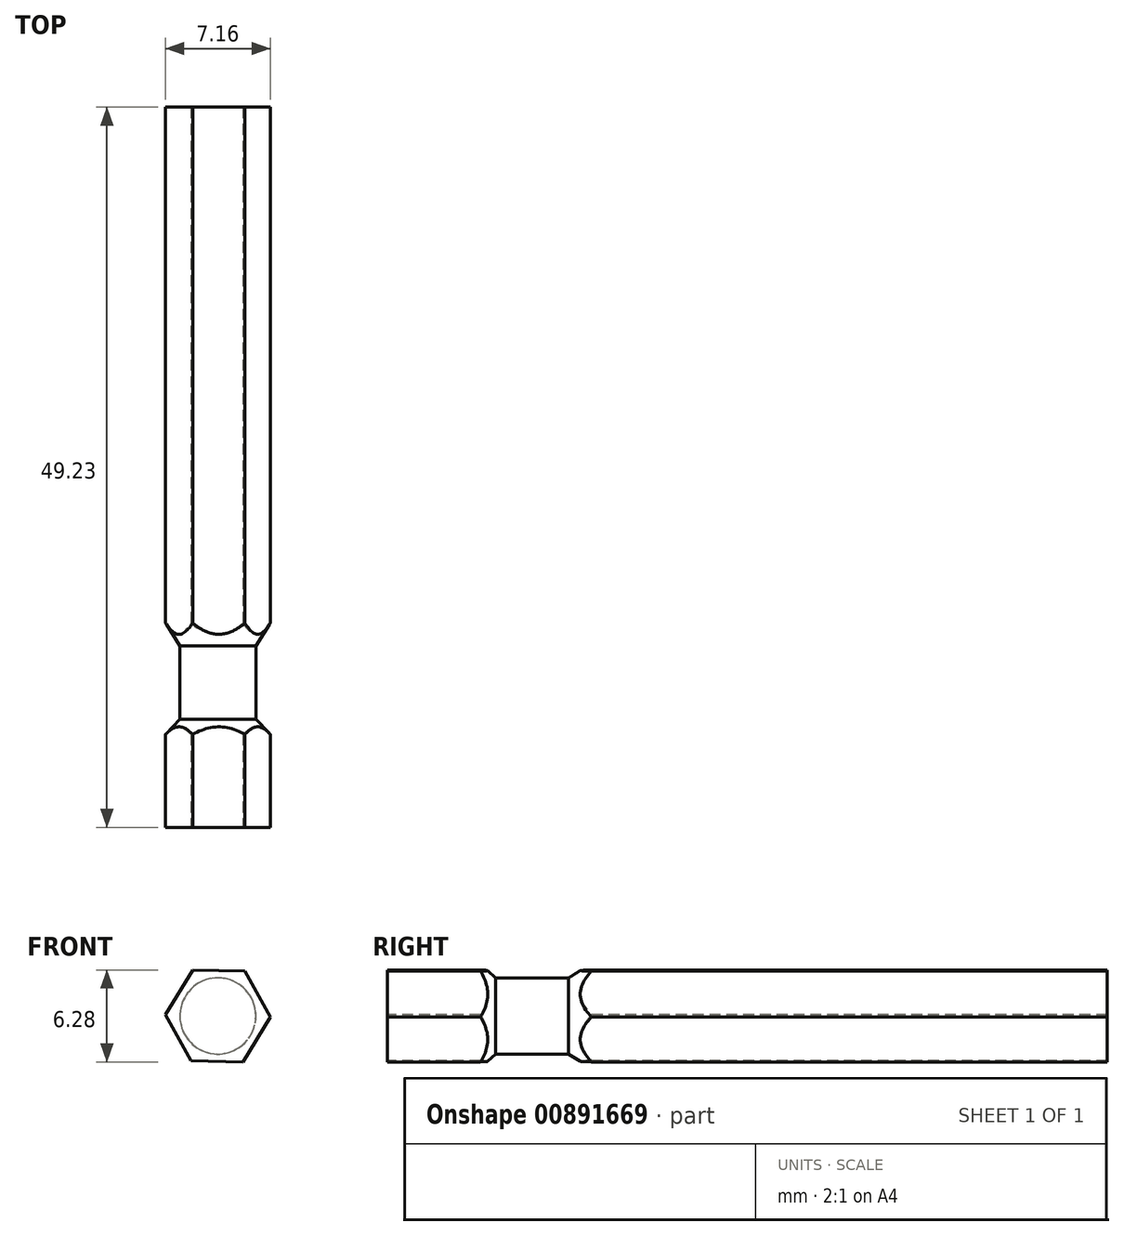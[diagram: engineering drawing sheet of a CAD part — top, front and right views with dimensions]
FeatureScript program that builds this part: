
annotation { "Feature Type Name" : "Feature", "Feature Type Description" : "" }
export const myFeature = defineFeature(function(context is Context, id is Id, definition is map)
    precondition{}
    {
        {
            var Q0;
            Q0=qCreatedBy(makeId("Top.planeOp"),FACE);
            var sketch = newSketch(context, id + "F0", { "sketchPlane" : qUnion([Q0])});
            skLineSegment(sketch, "E0.top", {"start": v(-3.75, -17.5) * mm, "end": v(3.75, -17.5) * mm});
            skLineSegment(sketch, "E0.left", {"start": v(-3.75, 17.5) * mm, "end": v(-3.75, -3.27) * mm});
            skLineSegment(sketch, "E0.right", {"start": v(3.75, 17.5) * mm, "end": v(3.75, -3.27) * mm});
            skPoint(sketch, "E0.middle", {"position": v(0, 0) * mm});
            skLineSegment(sketch, "E1", {"start": v(-2.6, -10.1) * mm, "end": v(2.6, -10.1) * mm});
            skLineSegment(sketch, "E2.bottom", {"start": v(2.6, -10.1) * mm, "end": v(-2.6, -10.1) * mm});
            skLineSegment(sketch, "E2.top", {"start": v(2.6, -5.1) * mm, "end": v(-2.6, -5.1) * mm});
            skLineSegment(sketch, "E2.left", {"start": v(2.6, -10.1) * mm, "end": v(2.6, -5.1) * mm});
            skLineSegment(sketch, "E2.right", {"start": v(-2.6, -10.1) * mm, "end": v(-2.6, -5.1) * mm});
            skLineSegment(sketch, "E3", {"start": v(-2.6, -5.1) * mm, "end": v(-3.75, -3.27) * mm});
            skLineSegment(sketch, "E4.MirrorCS", {"start": v(2.6, -5.1) * mm, "end": v(3.75, -3.27) * mm});
            skLineSegment(sketch, "E5.trimOffspring", {"start": v(-3.75, -11.31) * mm, "end": v(-3.75, -17.5) * mm});
            skLineSegment(sketch, "E6.trimOffspring", {"start": v(3.75, -11.31) * mm, "end": v(3.75, -17.5) * mm});
            skLineSegment(sketch, "E7", {"start": v(-2.6, -10.1) * mm, "end": v(-3.75, -11.31) * mm});
            skLineSegment(sketch, "E8.MirrorCS", {"start": v(2.6, -10.1) * mm, "end": v(3.75, -11.31) * mm});
            skLineSegment(sketch, "E9", {"start": v(-3.75, 17.5) * mm, "end": v(-3.75, 31.73) * mm});
            skLineSegment(sketch, "E10", {"start": v(-3.75, 31.73) * mm, "end": v(3.75, 31.73) * mm});
            skLineSegment(sketch, "E11", {"start": v(3.75, 31.73) * mm, "end": v(3.75, 17.5) * mm});
            skLineSegment(sketch, "E12", {"start": v(0, 31.73) * mm, "end": v(0, -17.5) * mm});
            skSolve(sketch);
        }
        {
            var Q0;
            Q0=makeQuery(id+"F0.imprint","IMPRINT",FACE,{"disambiguationData":[TD([[makeQuery(id+"F0.imprint","IMPRINT",EDGE,{"derivedFrom":sQuery(id+"F0.wireOp",EDGE,"E0.left")}),1.0]])]});
            var Q1;
            {var subQ0=sQuery(id+"F0.wireOp",EDGE,"E2.right");Q1=makeQuery(id+"F0.imprint","IMPRINT",FACE,{"disambiguationData":[TD([[makeQuery(id+"F0.imprint","IMPRINT",EDGE,{"derivedFrom":subQ0}),-1.0]])]});}
            var Q2;
            {var subQ1=sQuery(id+"F0.wireOp",EDGE,"E5.trimOffspring");Q2=makeQuery(id+"F0.imprint","IMPRINT",FACE,{"disambiguationData":[TD([[makeQuery(id+"F0.imprint","IMPRINT",EDGE,{"derivedFrom":subQ1}),1.0]])]});}
            var Q3;
            Q3=sQuery(id+"F0.wireOp",EDGE,"E12");
            revolve(context, id + "F1", {"surfaceOperationType" : NewSurfaceOperationType.NEW, "entities" : qUnion([Q0, Q1, Q2]), "axis" : qUnion([Q3]), "revolveType" : RevolveType.FULL});
        }
        {
            var Q0;
            Q0=makeQuery(id+"F1.opRevolve","SWEPT_FACE",FACE,{"disambiguationData":[OSD([sQuery(id+"F0.wireOp",EDGE,"E0.top")])]});
            var sketch = newSketch(context, id + "F2", { "sketchPlane" : qUnion([Q0])});
            skLineSegment(sketch, "E13.0", {"start": v(-1.72, 3.14) * mm, "end": v(1.86, 3.06) * mm});
            skLineSegment(sketch, "E13.1", {"start": v(1.86, 3.06) * mm, "end": v(3.58, -0.08) * mm});
            skLineSegment(sketch, "E13.2", {"start": v(3.58, -0.08) * mm, "end": v(1.72, -3.14) * mm});
            skLineSegment(sketch, "E13.3", {"start": v(1.72, -3.14) * mm, "end": v(-1.86, -3.06) * mm});
            skLineSegment(sketch, "E13.4", {"start": v(-1.86, -3.06) * mm, "end": v(-3.58, 0.08) * mm});
            skLineSegment(sketch, "E13.5", {"start": v(-3.58, 0.08) * mm, "end": v(-1.72, 3.14) * mm});
            skSolve(sketch);
        }
        {
            var Q0;
            Q0=makeQuery(id+"F2.imprint","IMPRINT",FACE,{"disambiguationData":[TD([[makeQuery(id+"F2.imprint","IMPRINT",EDGE,{"derivedFrom":sQuery(id+"F2.wireOp",EDGE,"E13.0")}),1.0]])]});
            extrude(context, id + "F3", {"entities" : qUnion([Q0]), "operationType" : NewBodyOperationType.REMOVE, "oppositeDirection" : true, "depth" : 65 * mm, "offsetDistance" : 25 * mm});
        }
    });
